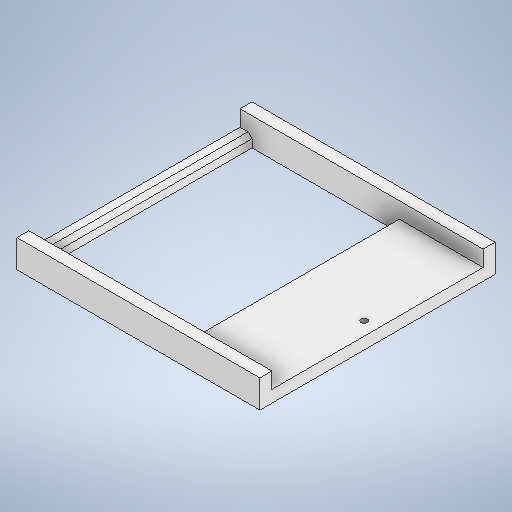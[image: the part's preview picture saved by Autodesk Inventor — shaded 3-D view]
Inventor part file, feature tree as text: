
AUTODESK INVENTOR PART (.ipt)
format: ipt  version: 2025 (Build 290162000, 162)  size: 334,336 bytes
history: native  units: in
note: dims shown in document units (in); Inventor stores cm internally (conversion verified against a paired STEP export)
features: sketch x4, extrude x3, hole x1, chamfer x1
ambient origin geometry x8: Origin, YZ Plane, XZ Plane, XY Plane, X Axis, Y Axis, Z Axis, Center Point
bodies: Solid1 (feature_tree)
feature tree (9):
  extrude  "Extrusion1"  Depth=2.4016in
  extrude  "Extrusion2"  Depth=2.0866in
  hole  "Hole1"  [1 undecoded]
  extrude  "Extrusion3"  Depth=1.4567in
  chamfer  "Chamfer1"  [1 undecoded]
  sketch  "Sketch1"  dims[d0=2.3228in d1=2.4016in]
  sketch  "Sketch2"  dims[d2=0.2756in d3=0.0in d4=2.0866in]
  sketch  "Sketch3"  dims[d5=0.1575in d6=0.0in d7=1.0689in d8=1.0689in]
  sketch  "Sketch4"  dims[d9=0.0617in d10=0.1575in d11=0.1732in d12=0.0787in d13=90.0deg d14=2.3622in d15=0.0in d16=1.4567in d17=0.0in d18=0.0in d19=0.1181in d20=0.0394in d21=0.0787in d22=45.0deg]
note: 2 required parameter values undecoded (feature->parameter linkage not recoverable at this tier; creation-order binding heuristic only, values carry confidence <= 0.55)
